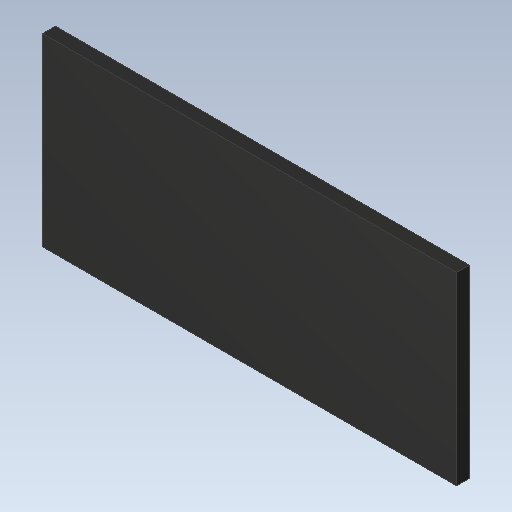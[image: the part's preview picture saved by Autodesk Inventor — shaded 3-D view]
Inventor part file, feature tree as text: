
AUTODESK INVENTOR PART (.ipt)
format: ipt  version: 2023 (Build 270158000, 158)  size: 91,136 bytes
history: imported  units: in
note: dims shown in document units (in); Inventor stores cm internally (conversion verified against a paired STEP export)
features: imported_body x1
ambient origin geometry x8: Origin, YZ Plane, XZ Plane, XY Plane, X Axis, Y Axis, Z Axis, Center Point
bodies: Solid1 (imported_parasolid), Body1 (imported_parasolid)
feature tree (1):
  imported_body  NMx_Import_Brep_tag  [imported B-rep: ~6 faces, bbox_mm=[3.2508, 1.4508, 0.1]]
